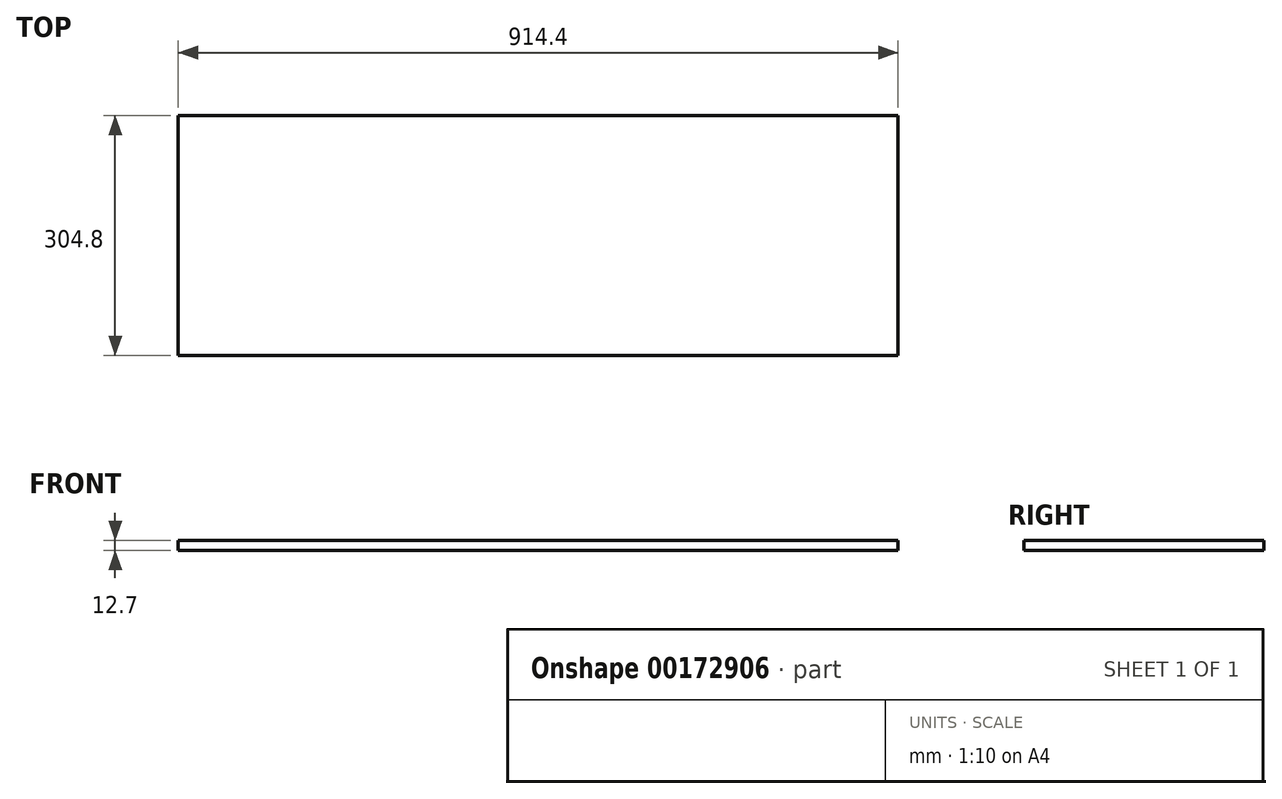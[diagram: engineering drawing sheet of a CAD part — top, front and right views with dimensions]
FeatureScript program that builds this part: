
annotation { "Feature Type Name" : "Feature", "Feature Type Description" : "" }
export const myFeature = defineFeature(function(context is Context, id is Id, definition is map)
    precondition{}
    {
        {
            var Q0;
            Q0=qCreatedBy(makeId("Top.planeOp"),FACE);
            var sketch = newSketch(context, id + "F0", { "sketchPlane" : qUnion([Q0])});
            skLineSegment(sketch, "E0.bottom", {"start": v(0, 0) * mm, "end": v(-914.4, 0) * mm});
            skLineSegment(sketch, "E0.top", {"start": v(0, 304.8) * mm, "end": v(-914.4, 304.8) * mm});
            skLineSegment(sketch, "E0.left", {"start": v(0, 0) * mm, "end": v(0, 304.8) * mm});
            skLineSegment(sketch, "E0.right", {"start": v(-914.4, 0) * mm, "end": v(-914.4, 304.8) * mm});
            skSolve(sketch);
        }
        {
            var Q0;
            Q0=makeQuery(id+"F0.imprint","IMPRINT",FACE,{"disambiguationData":[TD([[makeQuery(id+"F0.imprint","IMPRINT",EDGE,{"derivedFrom":sQuery(id+"F0.wireOp",EDGE,"E0.bottom")}),-1.0]])]});
            extrude(context, id + "F1", {"entities" : qUnion([Q0]), "depth" : 12.7 * mm});
        }
    });
